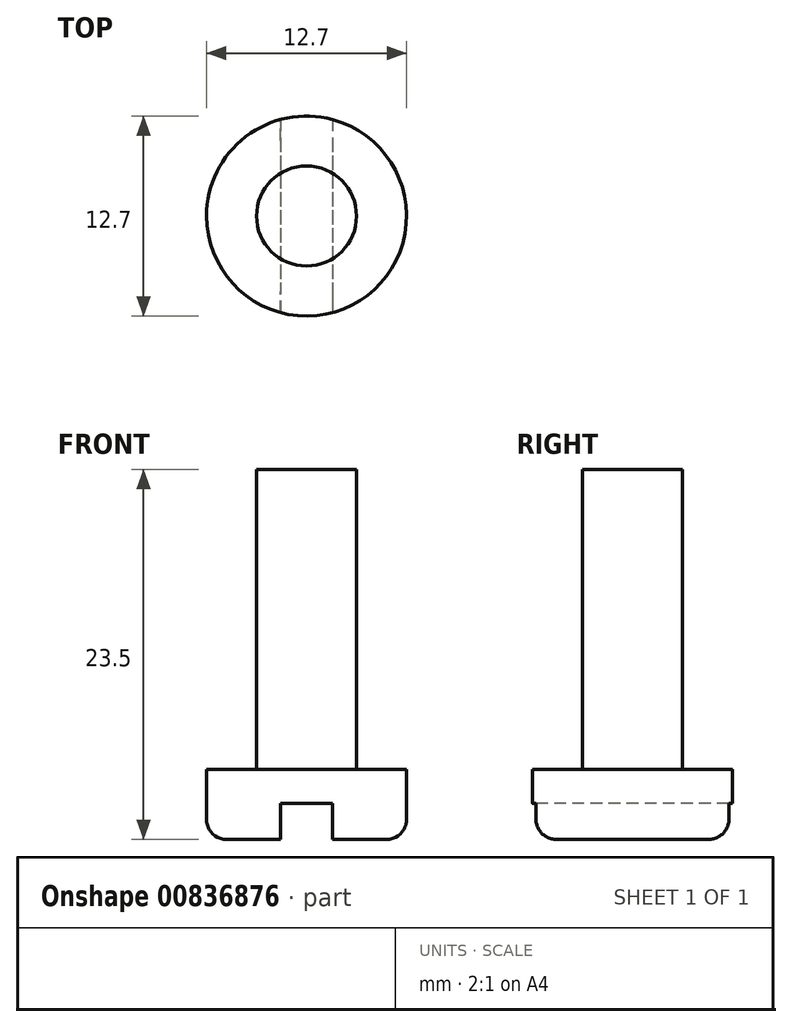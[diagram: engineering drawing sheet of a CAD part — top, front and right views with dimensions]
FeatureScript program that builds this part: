
annotation { "Feature Type Name" : "Feature", "Feature Type Description" : "" }
export const myFeature = defineFeature(function(context is Context, id is Id, definition is map)
    precondition{}
    {
        {
            var Q0;
            Q0=qCreatedBy(makeId("Top.planeOp"),FACE);
            var sketch = newSketch(context, id + "F0", { "sketchPlane" : qUnion([Q0])});
            skCircle(sketch, "E0", {"center": v(0, 0) * mm, "radius": 3.18 * mm});
            skSolve(sketch);
        }
        {
            var Q0;
            Q0 = qSketchRegion(id + "F0", true);
            extrude(context, id + "F1", {"entities" : qUnion([Q0]), "depth" : 19.05 * mm, "offsetDistance" : 25.4 * mm});
        }
        {
            var Q0;
            Q0=makeQuery(id+"F1.opExtrude","CAP_FACE",FACE,{"disambiguationData":[OSD([sQuery(id+"F0.wireOp",EDGE,"E0")])],"isStart":true});
            var sketch = newSketch(context, id + "F2", { "sketchPlane" : qUnion([Q0])});
            skCircle(sketch, "E1", {"center": v(0, 0) * mm, "radius": 6.35 * mm});
            skSolve(sketch);
        }
        {
            var Q0;
            Q0 = qSketchRegion(id + "F2", true);
            extrude(context, id + "F3", {"entities" : qUnion([Q0]), "operationType" : NewBodyOperationType.ADD, "depth" : 4.44 * mm, "offsetDistance" : 25.4 * mm});
        }
        {
            var Q0;
            Q0=makeQuery(id+"F3.opExtrude","CAP_FACE",FACE,{"disambiguationData":[OSD([sQuery(id+"F2.wireOp",EDGE,"E1")])],"isStart":false});
            var sketch = newSketch(context, id + "F4", { "sketchPlane" : qUnion([Q0])});
            skLineSegment(sketch, "E2.bottom", {"start": v(1.65, -13.27) * mm, "end": v(-1.65, -13.27) * mm});
            skLineSegment(sketch, "E2.top", {"start": v(1.65, 13.27) * mm, "end": v(-1.65, 13.27) * mm});
            skLineSegment(sketch, "E2.left", {"start": v(1.65, -13.27) * mm, "end": v(1.65, 13.27) * mm});
            skLineSegment(sketch, "E2.right", {"start": v(-1.65, -13.27) * mm, "end": v(-1.65, 13.27) * mm});
            skPoint(sketch, "E2.middle", {"position": v(0, 0) * mm});
            skSolve(sketch);
        }
        {
            var Q0;
            Q0 = qSketchRegion(id + "F4", true);
            extrude(context, id + "F5", {"entities" : qUnion([Q0]), "operationType" : NewBodyOperationType.REMOVE, "oppositeDirection" : true, "depth" : 2.3 * mm, "offsetDistance" : 25.4 * mm});
        }
        {
            var Q0;
            {var subQ0=sQuery(id+"F2.wireOp",EDGE,"E1");Q0=makeQuery(id+"F5.boolean.opBoolean","SPLIT",EDGE,{"disambiguationData":[TD([makeQuery(id+"F5.opExtrude","SWEPT_FACE",FACE,{"disambiguationData":[OSD([sQuery(id+"F4.wireOp",EDGE,"E2.right")])]})])],"derivedFrom":makeQuery(id+"F3.opExtrude","CAP_EDGE",EDGE,{"disambiguationData":[OSD([subQ0])],"isStart":false})});}
            var Q1;
            {var subQ0=sQuery(id+"F2.wireOp",EDGE,"E1");Q1=makeQuery(id+"F5.boolean.opBoolean","SPLIT",EDGE,{"disambiguationData":[TD([makeQuery(id+"F5.opExtrude","SWEPT_FACE",FACE,{"disambiguationData":[OSD([sQuery(id+"F4.wireOp",EDGE,"E2.left")])]})])],"derivedFrom":makeQuery(id+"F3.opExtrude","CAP_EDGE",EDGE,{"disambiguationData":[OSD([subQ0])],"isStart":false})});}
            fillet(context, id + "F6", {"entities" : qUnion([Q0, Q1]), "radius" : 1.27 * mm, "tangentPropagation" : true, "allowEdgeOverflow" : false});
        }
    });
